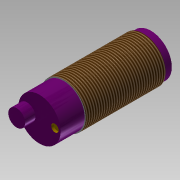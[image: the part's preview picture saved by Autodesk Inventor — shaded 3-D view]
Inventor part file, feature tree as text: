
AUTODESK INVENTOR PART (.ipt)
format: ipt  version: 2015 SP1 (Build 190203100, 203)  size: 188,928 bytes
history: native  units: mm
features: extrude x7, sketch x7, fillet x2, thread x1, projected_geometry x1
ambient origin geometry x8: Origin, YZ Plane, XZ Plane, XY Plane, X Axis, Y Axis, Z Axis, Center Point
bodies: Solid1 (feature_tree)
feature tree (18):
  extrude  "Extrusion1"  Depth=31.82mm TaperAngle=0.0deg
  thread  "Thread1"  [1 undecoded]
  extrude  "Extrusion2"  Depth=1.4mm
  extrude  "Extrusion3"  Depth=3.0mm TaperAngle=0.0deg
  fillet  "Fillet1"  Radius=3.0mm
  fillet  "Fillet2"  Radius=3.0mm
  extrude  "Extrusion4"  Depth=9.6mm TaperAngle=0.0deg
  sketch  "Sketch5"  dims[d22=3.0mm d23=6.71mm]
  extrude  "Extrusion5"  Depth=3.0mm
  extrude  "Extrusion6"  Depth=4.1mm TaperAngle=0.0deg
  sketch  "Sketch6"  dims[d24=1.0mm d25=0.0mm d26=4.1mm d27=0.0mm]
  extrude  "Extrusion7"  [1 undecoded]
  sketch  "Sketch1"  dims[d0=17.8mm d1=31.82mm d2=0.0mm d3=10.0mm d4=0.0mm]
  sketch  "Sketch2"  dims[d5=16.74mm d6=1.4mm]
  sketch  "Sketch3"  dims[d7=3.0mm d8=0.0mm d15=2.0mm d16=0.0mm d17=3.0mm d18=3.0mm]
  sketch  "Sketch4"  dims[d19=16.89mm d20=9.6mm d21=0.0mm]
  sketch  "Sketch7"  dims[d28=200.0mm d29=0.0mm]
  projected_geometry  "Projected Loop2"
note: 2 required parameter values undecoded (feature->parameter linkage not recoverable at this tier; creation-order binding heuristic only, values carry confidence <= 0.55)
